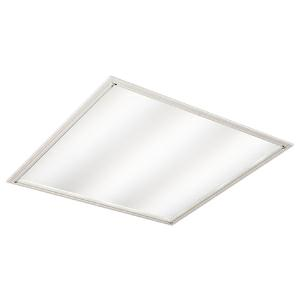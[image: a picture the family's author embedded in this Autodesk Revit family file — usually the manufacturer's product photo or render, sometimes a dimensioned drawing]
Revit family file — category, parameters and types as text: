
# Revit family: 3f_filippi_-_l_320_lgs_3f_filippi_-_22709_-_l_324x10w-940_led_lgs_596x596
name_source: partatom
category: Lighting Fixtures
units: mm (PartAtom-declared; Revit-internal decimal feet)

## family parameters
Cut with Voids When Loaded = No
Host = Face
Light Source = No
Part Type = Normal
Room Calculation Point = No
Round Connector Dimension = Use Diameter
Shared = No

## types (1)
- 3F Filippi - L 320 LGS (1 x LED, 3327 lm, 45 W, 4000 K)
    Apparent Load = 45 VA
    Approval mark = ENEC
    CIE Flux Codes = 62 88 97 100 100
    Color Rendering = 90
    Color Temperature = 4000 K
    Control Gear = Electronic ballast
    Default Elevation = 1800 mm
    Description = ILLUMINOTECHNICAL
Luminous efficiency 100% (DLOR 100%, ULOR 0%).
Initial luminous flux of the luminaire 3327 lm.
Direct symmetric distribution.
Installation Interdistance Transv.D = 1.16 x hu - Long.D = 1.16 x hu.
Average luminance <3000 cd/m² for radial angles >65°.
Tabular UGR (CIE 117 - 4H-8H; S=0.25H; 70/50/20): RUG 17.9 - 17.9.
Beam angle: 85° - 84°.
Luminous efficacy 74 lm/W.
Lifetime (L93/B10): 30000 h. (tq+25°C)
Lifetime (L90/B10): 50000 h. (tq+25°C)
Lifetime (L85/B10): 80000 h. (tq+25°C)
Lifetime (L80/B10): 100000 h. (tq+25°C)
Sudden decreased luminous flux after 50000 hours: 0% (C0).
Photobiological safety in compliance with IEC/TR 62778: RG0 risk exempt, (IEC 62471).
In compliance with IEC/EN 62722-2-1 - IEC/EN 62717 standards.

SOURCE
4 linear LED modules 10W/940.
Energy efficiency class (UE 2019/2020 - UE 2019/2015): E.
CIE 13.3 Colour rendering index: CRI >90 (R9 >50%).
IES TM-30 Fidelity Index: Rf = 92 Rg = 101.
CCT nominal colour temperature 4000 K.
Colour initial tolerance (MacAdam): SDCM 2.

MECHANICAL
Housing in hot-galvanised steel, painted in white polyester.
Micro-prismatic flat diffuser in transparent methacrylate (PMMA), multilenticular exterior, anti-glare, locked to the white painted aluminium perimetral frame, sealing gasket, hinged opening.
Anti-glare opal polycarbonate filter for brightness uniformity.
Luminaire with limited surface temperature. - D - (EN 60598-2-24)
Dimensions: 596x596 mm, height 80 mm. Weight 4.82 kg.
IP54 protection degree for exposed part, IP20 for recessed part.
Mechanical strength to impacts IK06 (1 joule).
Glow-wire test resistance 650°C.

ELECTRICAL
Halogen Free electronic wiring 230V-50/60Hz, power factor 0.95, THD <25%, constant output current, SELV, class I, 1 driver.
Power of the luminaire 45 W.
CE - IEC 60598-1 - EN 60598-1.
SAFE FLICKER: PstLM=<1 and SVM=<0.4 (IEC TR 61547-1 and IEC TR 63158), to ensure a more comfortable and safe light.
Luminaire compliant with EN 60598-2-22 for power supply from a centralised emergency system CPSS (Central Power Supply System), not incorporated in the luminaire - high risk areas excluded. The default power and flux are 100% in AC and 100% in DC.
Ambient temperature from 0°C to +25°C.
Temperature class T6 max 85°C.
Relative humidity UR: <85%.

INSTALLATION
Lay-in recessed fitting.
On request: pull-up recessed fitting with brackets.
False ceiling carving: 580x580 mm.
All accessories dedicated to this product are available on the Catalog and on our website www.3F-Filippi.com.

APPLICATIONS
Environments: sterilized, aseptic.
In environments with VDU's, managerial offices and staterooms, environments involving accurate visual tasks where a diffused and soft light for an optimum visual comfort and the source total shielding are required.

WARNING
Luminaire designed for disposal/recycling at end-of-life.
Replaceable (LED only) light source by a professional. Replaceable control gear by a professional.
    Height = 0 mm  [stored 0 ft]
    Lamp = 1 x LED
    Lamp Light Flux = 3327 lm
    Lamp Power = 45 W
    Lamp count = 1
    Length = 596 mm
    Lifetime = 50000 h
    Luminous efficacy = 74 lm/W
    Manufacturer = 3F Filippi
    ModVariant = No
    Model = 3F Filippi - 22709 - L 324x10W-940 LED LGS 596x596
    Mounting Place = Ceiling
    Mounting Type = Recessed
    Number of Poles = 1
    OnlyDefault = Yes
    Power Factor = 1
    Product Name = 3F Filippi - L 320 LGS
    Product group = recessed luminaire
    ProductGroupID = 4
    Protection Class = Protection class I
    Protection Degree = IP 20
    RLX_Detail_Level = 1
    RLX_Emergency_Light_Flux = 0 lm
    RLX_Emergency_Type = 0
    RLX_Emergency_Type_DB = No
    RlxData = <blob elided: 34065 chars, md5=59bc946e>
    Socket = socket
    Standby Power = 0 W
    System Light Flux = 3327 lm
    System Power = 45 W
    Type Comments = Product without accessories
    Type Image = 3ffilippi_l_320_led_lgs.jpg
    URL = http://relux.com
    VarID = ---
    Voltage = 0 V
    Weight = 0.00 kg
    Width = 596 mm

note: [stored X ft] marks values corroborated as IEEE doubles in the binary element streams (Revit-internal decimal feet)

## geometry (parser evidence)
native form markers: Blend x4, Sweep x10
no freeform markers — native parametric forms only
